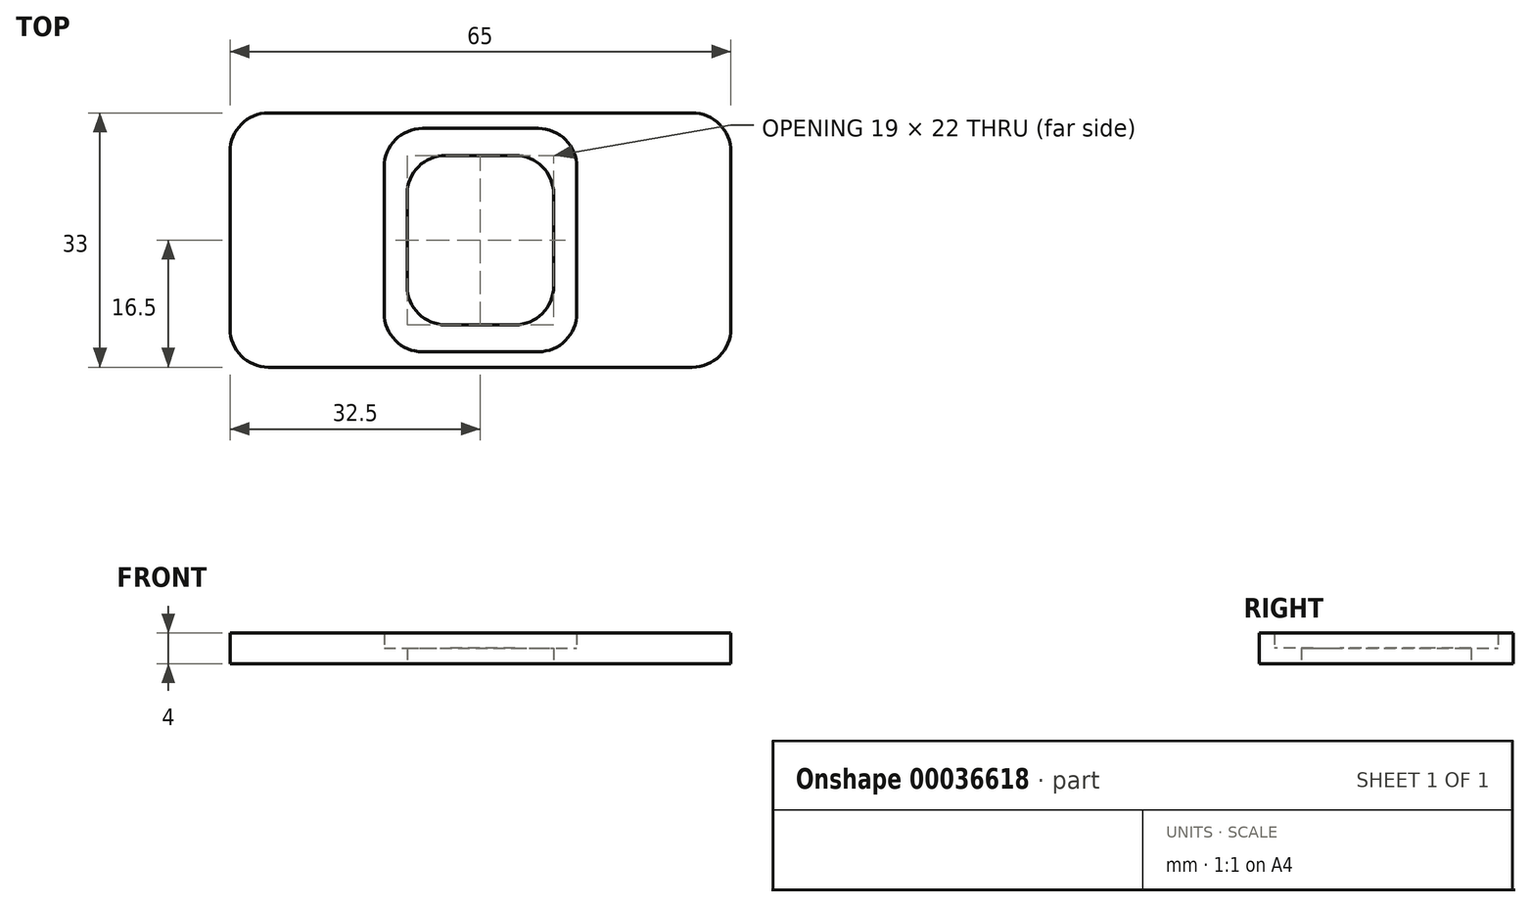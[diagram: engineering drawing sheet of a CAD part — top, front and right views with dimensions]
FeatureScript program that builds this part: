
annotation { "Feature Type Name" : "Feature", "Feature Type Description" : "" }
export const myFeature = defineFeature(function(context is Context, id is Id, definition is map)
    precondition{}
    {
        {
            var Q0;
            Q0=qCreatedBy(makeId("Top.planeOp"),FACE);
            var sketch = newSketch(context, id + "F0", { "sketchPlane" : qUnion([Q0])});
            skLineSegment(sketch, "E0.rect.bottom", {"start": v(27.5, 16.5) * mm, "end": v(-27.5, 16.5) * mm});
            skLineSegment(sketch, "E0.rect.top", {"start": v(27.5, -16.5) * mm, "end": v(-27.5, -16.5) * mm});
            skLineSegment(sketch, "E0.rect.left", {"start": v(32.5, 11.5) * mm, "end": v(32.5, -11.5) * mm});
            skLineSegment(sketch, "E0.rect.right", {"start": v(-32.5, 11.5) * mm, "end": v(-32.5, -11.5) * mm});
            skPoint(sketch, "E0.rect.middle", {"position": v(0, 0) * mm});
            skLineSegment(sketch, "E1.rect.bottom", {"start": v(7.5, 14.5) * mm, "end": v(-7.5, 14.5) * mm});
            skLineSegment(sketch, "E1.rect.top", {"start": v(7.5, -14.5) * mm, "end": v(-7.5, -14.5) * mm});
            skLineSegment(sketch, "E1.rect.left", {"start": v(12.5, 9.5) * mm, "end": v(12.5, -9.5) * mm});
            skLineSegment(sketch, "E1.rect.right", {"start": v(-12.5, 9.5) * mm, "end": v(-12.5, -9.5) * mm});
            skLineSegment(sketch, "E2.rect.bottom", {"start": v(4.5, 11) * mm, "end": v(-4.5, 11) * mm});
            skLineSegment(sketch, "E2.rect.top", {"start": v(4.5, -11) * mm, "end": v(-4.5, -11) * mm});
            skLineSegment(sketch, "E2.rect.left", {"start": v(9.5, 6) * mm, "end": v(9.5, -6) * mm});
            skLineSegment(sketch, "E2.rect.right", {"start": v(-9.5, 6) * mm, "end": v(-9.5, -6) * mm});
            skPoint(sketch, "E3.visualSharp", {"position": v(-32.5, -16.5) * mm});
            skArc(sketch, "E3.filletArc", {"start": v(-32.5, -11.5) * mm, "mid": v(-31.04, -15.04) * mm, "end": v(-27.5, -16.5) * mm});
            skPoint(sketch, "E4.visualSharp", {"position": v(32.5, -16.5) * mm});
            skArc(sketch, "E4.filletArc", {"start": v(27.5, -16.5) * mm, "mid": v(31.04, -15.04) * mm, "end": v(32.5, -11.5) * mm});
            skPoint(sketch, "E5.visualSharp", {"position": v(32.5, 16.5) * mm});
            skArc(sketch, "E5.filletArc", {"start": v(32.5, 11.5) * mm, "mid": v(31.04, 15.04) * mm, "end": v(27.5, 16.5) * mm});
            skPoint(sketch, "E6.visualSharp", {"position": v(-32.5, 16.5) * mm});
            skArc(sketch, "E6.filletArc", {"start": v(-27.5, 16.5) * mm, "mid": v(-31.04, 15.04) * mm, "end": v(-32.5, 11.5) * mm});
            skPoint(sketch, "E7.visualSharp", {"position": v(-12.5, 14.5) * mm});
            skArc(sketch, "E7.filletArc", {"start": v(-7.5, 14.5) * mm, "mid": v(-11.04, 13.04) * mm, "end": v(-12.5, 9.5) * mm});
            skPoint(sketch, "E8.visualSharp", {"position": v(-12.5, -14.5) * mm});
            skArc(sketch, "E8.filletArc", {"start": v(-12.5, -9.5) * mm, "mid": v(-11.04, -13.04) * mm, "end": v(-7.5, -14.5) * mm});
            skPoint(sketch, "E9.visualSharp", {"position": v(12.5, -14.5) * mm});
            skArc(sketch, "E9.filletArc", {"start": v(7.5, -14.5) * mm, "mid": v(11.04, -13.04) * mm, "end": v(12.5, -9.5) * mm});
            skPoint(sketch, "E10.visualSharp", {"position": v(12.5, 14.5) * mm});
            skArc(sketch, "E10.filletArc", {"start": v(12.5, 9.5) * mm, "mid": v(11.04, 13.04) * mm, "end": v(7.5, 14.5) * mm});
            skPoint(sketch, "E11.visualSharp", {"position": v(9.5, 11) * mm});
            skArc(sketch, "E11.filletArc", {"start": v(9.5, 6) * mm, "mid": v(8.04, 9.54) * mm, "end": v(4.5, 11) * mm});
            skPoint(sketch, "E12.visualSharp", {"position": v(9.5, -11) * mm});
            skArc(sketch, "E12.filletArc", {"start": v(4.5, -11) * mm, "mid": v(8.04, -9.54) * mm, "end": v(9.5, -6) * mm});
            skPoint(sketch, "E13.visualSharp", {"position": v(-9.5, -11) * mm});
            skArc(sketch, "E13.filletArc", {"start": v(-9.5, -6) * mm, "mid": v(-8.04, -9.54) * mm, "end": v(-4.5, -11) * mm});
            skPoint(sketch, "E14.visualSharp", {"position": v(-9.5, 11) * mm});
            skArc(sketch, "E14.filletArc", {"start": v(-4.5, 11) * mm, "mid": v(-8.04, 9.54) * mm, "end": v(-9.5, 6) * mm});
            skSolve(sketch);
        }
        {
            var Q0;
            Q0=makeQuery(id+"F0.imprint","IMPRINT",FACE,{"disambiguationData":[TD([[makeQuery(id+"F0.imprint","IMPRINT",EDGE,{"derivedFrom":sQuery(id+"F0.wireOp",EDGE,"E0.rect.bottom")}),1.0]])]});
            var Q1;
            Q1=makeQuery(id+"F0.imprint","IMPRINT",FACE,{"disambiguationData":[TD([[makeQuery(id+"F0.imprint","IMPRINT",EDGE,{"derivedFrom":sQuery(id+"F0.wireOp",EDGE,"E1.rect.bottom")}),1.0]])]});
            extrude(context, id + "F1", {"entities" : qUnion([Q0, Q1]), "depth" : 2 * mm});
        }
        {
            var Q0;
            Q0=makeQuery(id+"F0.imprint","IMPRINT",FACE,{"disambiguationData":[TD([[makeQuery(id+"F0.imprint","IMPRINT",EDGE,{"derivedFrom":sQuery(id+"F0.wireOp",EDGE,"E0.rect.bottom")}),1.0]])]});
            extrude(context, id + "F2", {"entities" : qUnion([Q0]), "operationType" : NewBodyOperationType.ADD, "depth" : 4 * mm});
        }
    });
